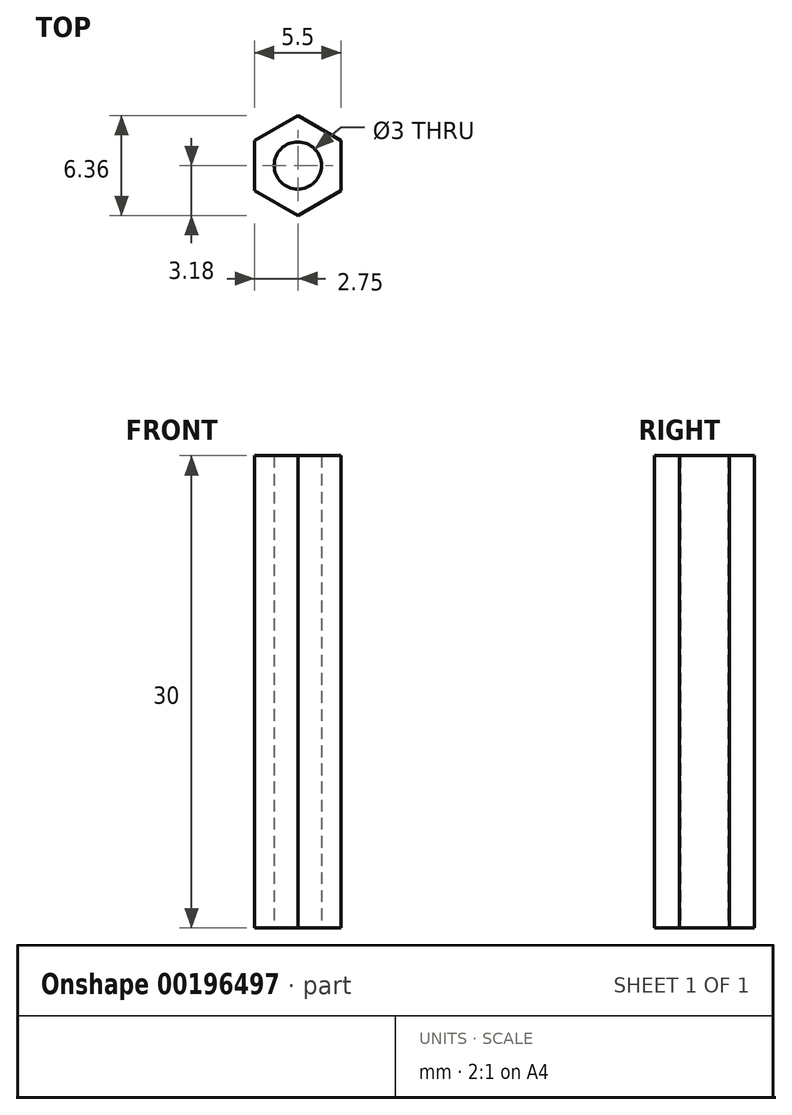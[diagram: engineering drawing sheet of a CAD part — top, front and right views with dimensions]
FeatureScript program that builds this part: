
annotation { "Feature Type Name" : "Feature", "Feature Type Description" : "" }
export const myFeature = defineFeature(function(context is Context, id is Id, definition is map)
    precondition{}
    {
        {
            var Q0;
            Q0=qCreatedBy(makeId("Top.planeOp"),FACE);
            var sketch = newSketch(context, id + "F0", { "sketchPlane" : qUnion([Q0])});
            skCircle(sketch, "E0", {"center": v(0, 0) * mm, "radius": 1.5 * mm});
            skCircle(sketch, "E1.cCircle", {"center": v(0, 0) * mm, "radius": 2.75 * mm, "construction": true});
            skLineSegment(sketch, "E1.0", {"start": v(2.75, 1.59) * mm, "end": v(2.75, -1.59) * mm});
            skLineSegment(sketch, "E1.1", {"start": v(2.75, -1.59) * mm, "end": v(0, -3.18) * mm});
            skLineSegment(sketch, "E1.2", {"start": v(0, -3.18) * mm, "end": v(-2.75, -1.59) * mm});
            skLineSegment(sketch, "E1.3", {"start": v(-2.75, -1.59) * mm, "end": v(-2.75, 1.59) * mm});
            skLineSegment(sketch, "E1.4", {"start": v(-2.75, 1.59) * mm, "end": v(0, 3.18) * mm});
            skLineSegment(sketch, "E1.5", {"start": v(0, 3.18) * mm, "end": v(2.75, 1.59) * mm});
            skPoint(sketch, "E1.0.midPoint", {"position": v(2.75, 0) * mm});
            skSolve(sketch);
        }
        {
            var Q0;
            Q0=makeQuery(id+"F0.imprint","IMPRINT",FACE,{"disambiguationData":[TD([[makeQuery(id+"F0.imprint","IMPRINT",EDGE,{"derivedFrom":sQuery(id+"F0.wireOp",EDGE,"E0")}),-1.0]])]});
            extrude(context, id + "F1", {"entities" : qUnion([Q0]), "depth" : 30 * mm});
        }
    });
